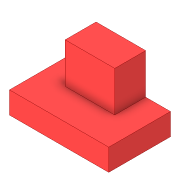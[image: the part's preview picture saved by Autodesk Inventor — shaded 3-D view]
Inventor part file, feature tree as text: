
AUTODESK INVENTOR PART (.ipt)
format: ipt  version: 2018.3 (Build 223284000, 284)  size: 101,888 bytes
history: native  units: in
note: dims shown in document units (in); Inventor stores cm internally (conversion verified against a paired STEP export)
features: extrude x2, sketch x2
ambient origin geometry x8: Origin, YZ Plane, XZ Plane, XY Plane, X Axis, Y Axis, Z Axis, Center Point
bodies: Solid1 (feature_tree)
feature tree (4):
  extrude  "Extrusion1"  Depth=0.5807in
  extrude  "Extrusion2"  Depth=0.2318in
  sketch  "Sketch1"  dims[d0=0.9268in d1=0.5807in]
  sketch  "Sketch2"  dims[d2=0.5768in d3=0.0in d4=0.2318in d5=0.232in d6=0.3768in d7=0.0in]
